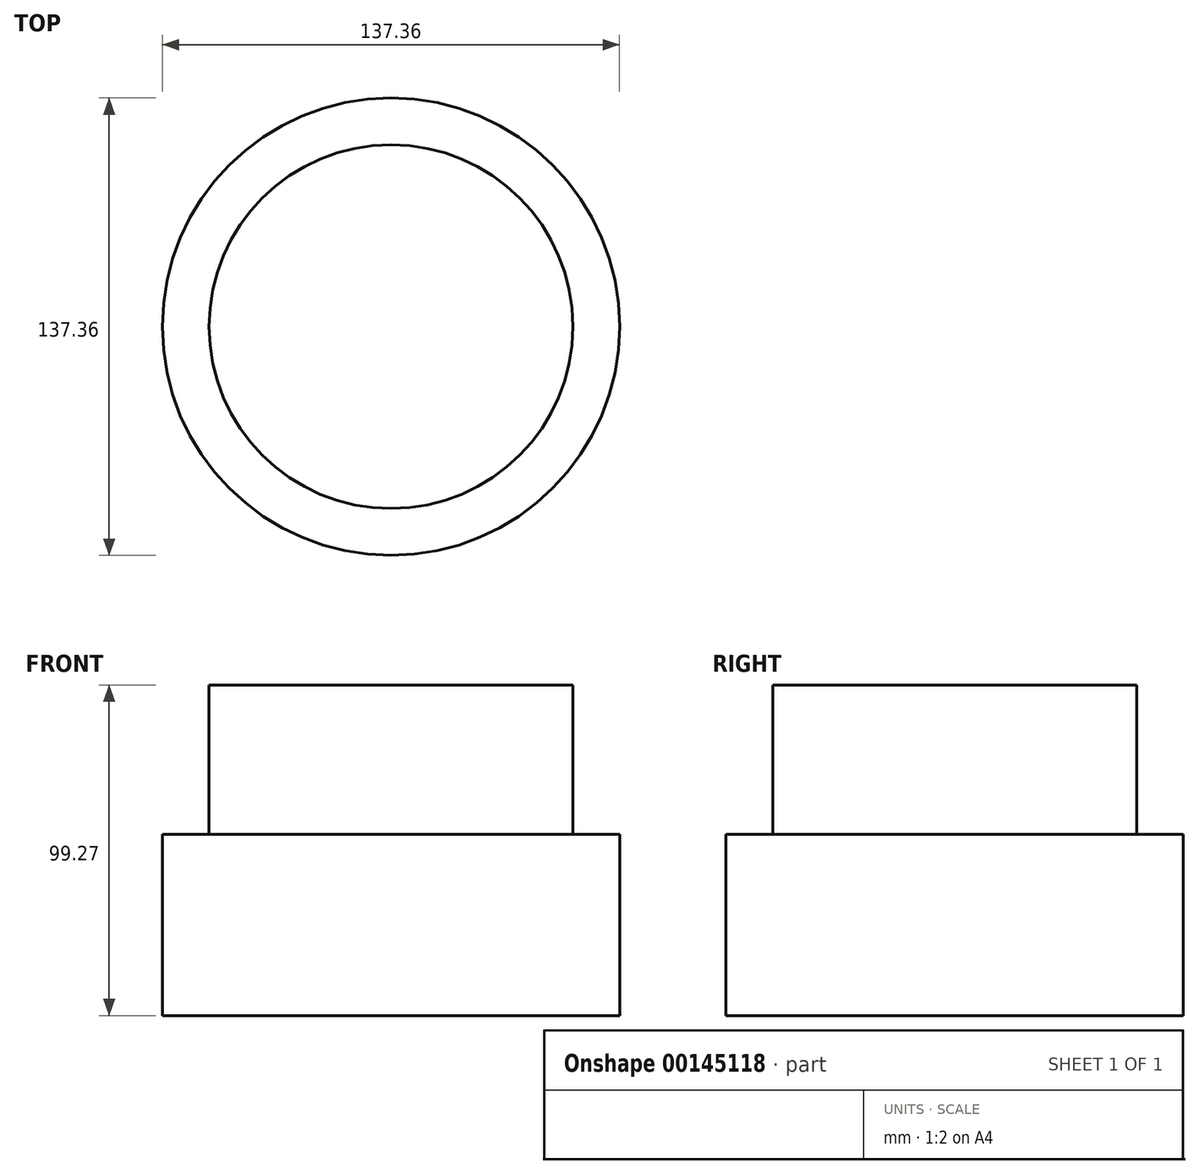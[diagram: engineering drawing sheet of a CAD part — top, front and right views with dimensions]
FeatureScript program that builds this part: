
annotation { "Feature Type Name" : "Feature", "Feature Type Description" : "" }
export const myFeature = defineFeature(function(context is Context, id is Id, definition is map)
    precondition{}
    {
        {
            var Q0;
            Q0=qCreatedBy(makeId("Top.planeOp"),FACE);
            var sketch = newSketch(context, id + "F0", { "sketchPlane" : qUnion([Q0])});
            skCircle(sketch, "E0", {"center": v(0, 0) * mm, "radius": 68.68 * mm});
            skSolve(sketch);
        }
        {
            var Q0;
            Q0=makeQuery(id+"F0.imprint","IMPRINT",FACE,{"disambiguationData":[TD([[makeQuery(id+"F0.imprint","IMPRINT",EDGE,{"derivedFrom":sQuery(id+"F0.wireOp",EDGE,"E0")}),1.0]])]});
            extrude(context, id + "F1", {"entities" : qUnion([Q0]), "depth" : 54.43 * mm});
        }
        {
            var Q0;
            Q0=makeQuery(id+"F0.imprint","IMPRINT",FACE,{"disambiguationData":[TD([[makeQuery(id+"F0.imprint","IMPRINT",EDGE,{"derivedFrom":sQuery(id+"F0.wireOp",EDGE,"E0")}),1.0]])]});
            var sketch = newSketch(context, id + "F2", { "sketchPlane" : qUnion([Q0])});
            skCircle(sketch, "E1", {"center": v(0, 0) * mm, "radius": 54.65 * mm});
            skSolve(sketch);
        }
        {
            var Q0;
            Q0=makeQuery(id+"F2.imprint","IMPRINT",FACE,{"disambiguationData":[TD([[makeQuery(id+"F2.imprint","IMPRINT",EDGE,{"derivedFrom":sQuery(id+"F2.wireOp",EDGE,"E1")}),1.0]])]});
            extrude(context, id + "F3", {"entities" : qUnion([Q0]), "operationType" : NewBodyOperationType.ADD, "depth" : 99.27 * mm});
        }
    });
